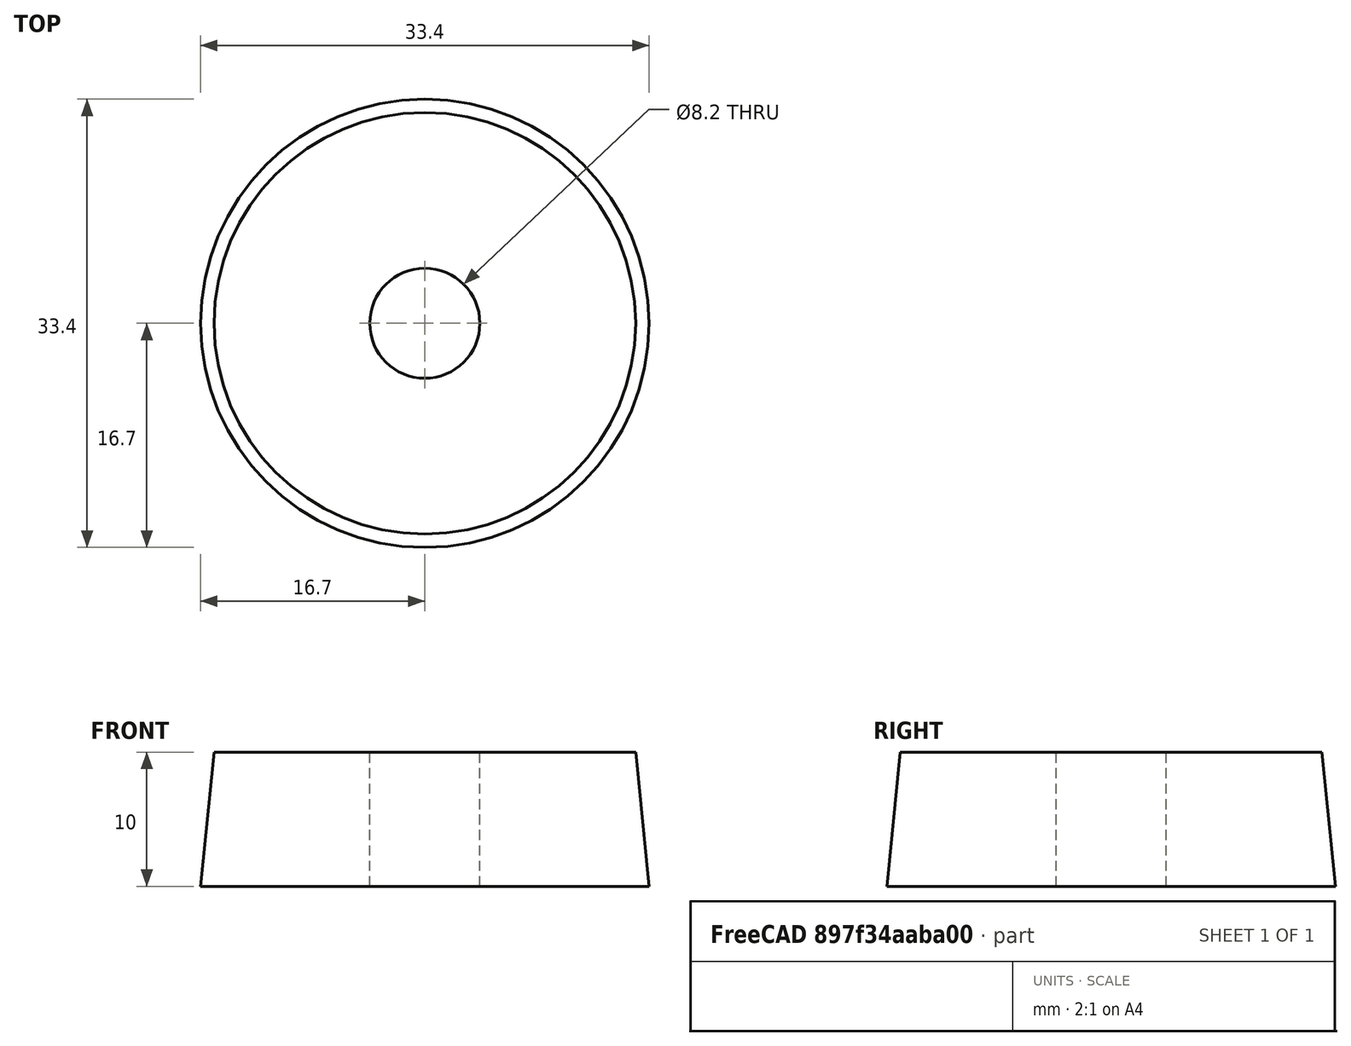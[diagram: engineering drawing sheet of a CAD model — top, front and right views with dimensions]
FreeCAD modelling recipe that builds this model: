
FCSTD DOCUMENT  (FreeCAD 1.0R39109 (Git))
Label: mandrel_wedge_32
License: All rights reserved
LicenseURL: http://en.wikipedia.org/wiki/All_rights_reserved
objects: Sketcher::SketchObject×1, PartDesign::Revolution×1, PartDesign::Body×1
note: 6 computed .brp shape members not serialized (recipe doc carries the construction recipe); baked Part::Feature solids carry a one-line shape summary decoded from their .brp

FEATURE [Sketcher::SketchObject] Sketch
  ArcFitTolerance = 1e-06
  AttachmentSupport = -> [XZ_Plane]
  FullyConstrained = true
  MakeInternals = false
  MapMode = 5
  Placement = pos=(0,0,0) rot=(1,0,0;1.5708rad)
  sketch-geometry (4):
    g0: LineSegment StartX=4.1 StartY=0 StartZ=0 EndX=4.1 EndY=10 EndZ=0
    g1: LineSegment StartX=4.1 StartY=10 StartZ=0 EndX=15.7 EndY=10 EndZ=0
    g2: LineSegment StartX=15.7 StartY=10 StartZ=0 EndX=16.7 EndY=0 EndZ=0
    g3: LineSegment StartX=16.7 StartY=0 StartZ=0 EndX=4.1 EndY=0 EndZ=0
  constraints (12):
    c: PointOnObject(g0,g-1)
    c: Vertical(g0)
    c: Coincident(g0,g1)
    c: Horizontal(g1)
    c: Coincident(g1,g2)
    c: Coincident(g2,g3)
    c: Coincident(g3,g0)
    c: Horizontal(g3)
    c: DistanceX(g-1,g0) = 4.1
    c: DistanceY(g0,g0) = 10
    c: DistanceX(g3,g3) = 12.6
    c: DistanceX(g1,g1) = 11.6
FEATURE [PartDesign::Revolution] Revolution
  Angle = 360
  Angle2 = 60
  Axis = (0,2e-16,1)
  Base = (0,0,0)
  Placement = pos=(0,0,0) rot=(1,0,0;1.5708rad)
  Profile = -> Sketch
  ReferenceAxis = -> Sketch [V_Axis]
  Refine = true
  Reversed = true
  Suppressed = false
  Type = 0
FEATURE [PartDesign::Body] Body
  AllowCompound = false
  Group = -> [Sketch,Revolution]
  Origin = -> Origin
  Tip = -> Revolution
